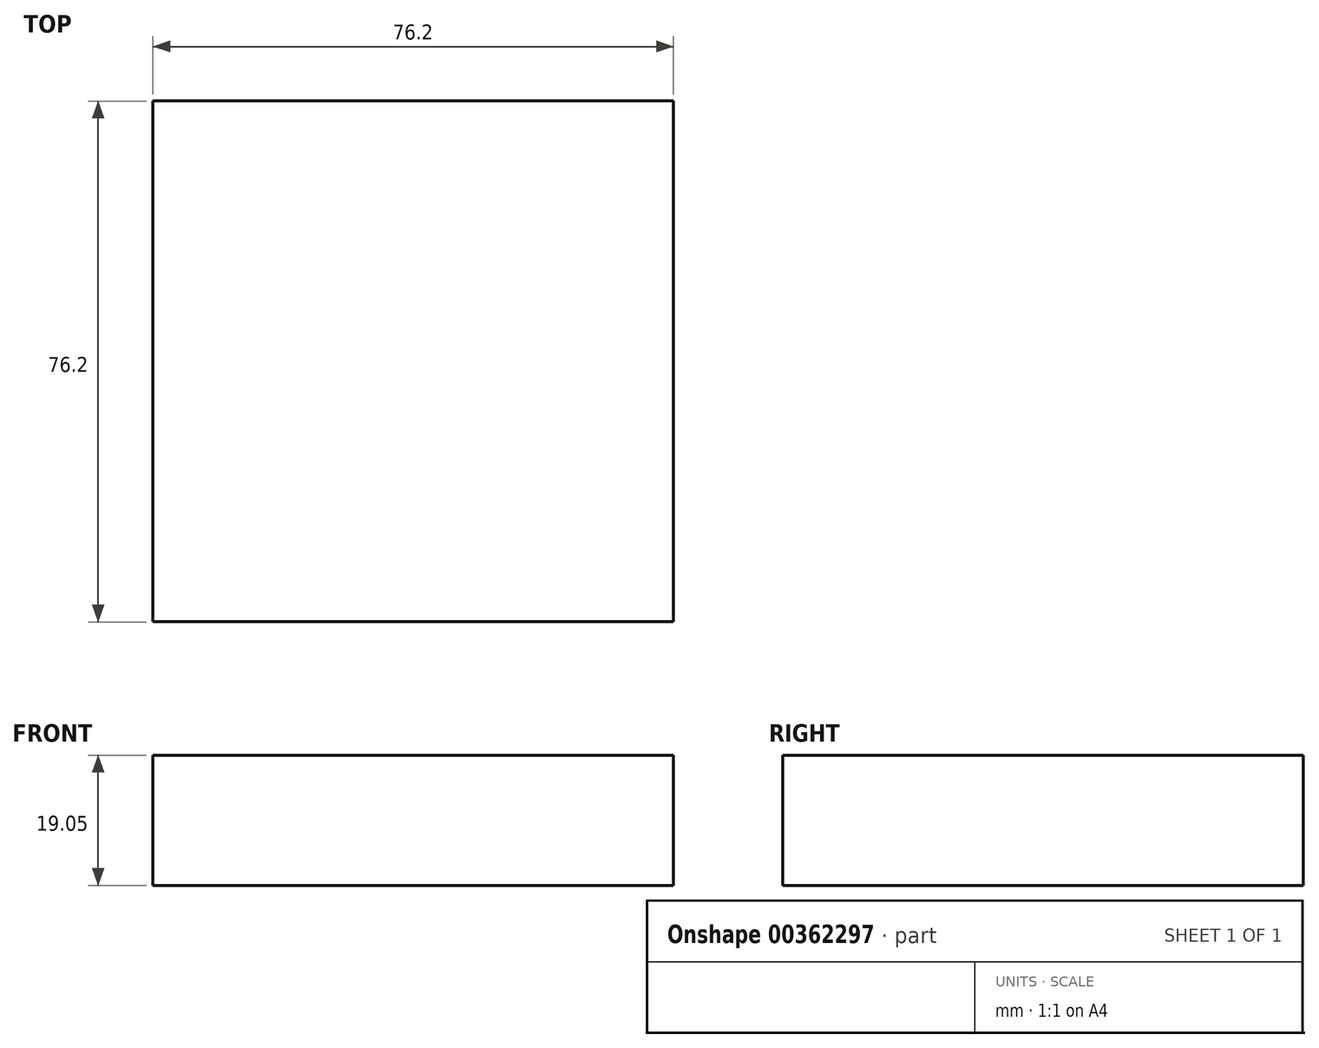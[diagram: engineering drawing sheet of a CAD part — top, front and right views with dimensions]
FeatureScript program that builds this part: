
annotation { "Feature Type Name" : "Feature", "Feature Type Description" : "" }
export const myFeature = defineFeature(function(context is Context, id is Id, definition is map)
    precondition{}
    {
        {
            var Q0;
            Q0=qCreatedBy(makeId("Top.planeOp"),FACE);
            var sketch = newSketch(context, id + "F0", { "sketchPlane" : qUnion([Q0])});
            skLineSegment(sketch, "E0.bottom", {"start": v(-58.34, 44.5) * mm, "end": v(17.86, 44.5) * mm});
            skLineSegment(sketch, "E0.top", {"start": v(-58.34, -31.7) * mm, "end": v(17.86, -31.7) * mm});
            skLineSegment(sketch, "E0.left", {"start": v(-58.34, 44.5) * mm, "end": v(-58.34, -31.7) * mm});
            skLineSegment(sketch, "E0.right", {"start": v(17.86, 44.5) * mm, "end": v(17.86, -31.7) * mm});
            skSolve(sketch);
        }
        {
            var Q0;
            Q0 = qSketchRegion(id + "F0", true);
            extrude(context, id + "F1", {"entities" : qUnion([Q0]), "depth" : 19.05 * mm});
        }
    });
